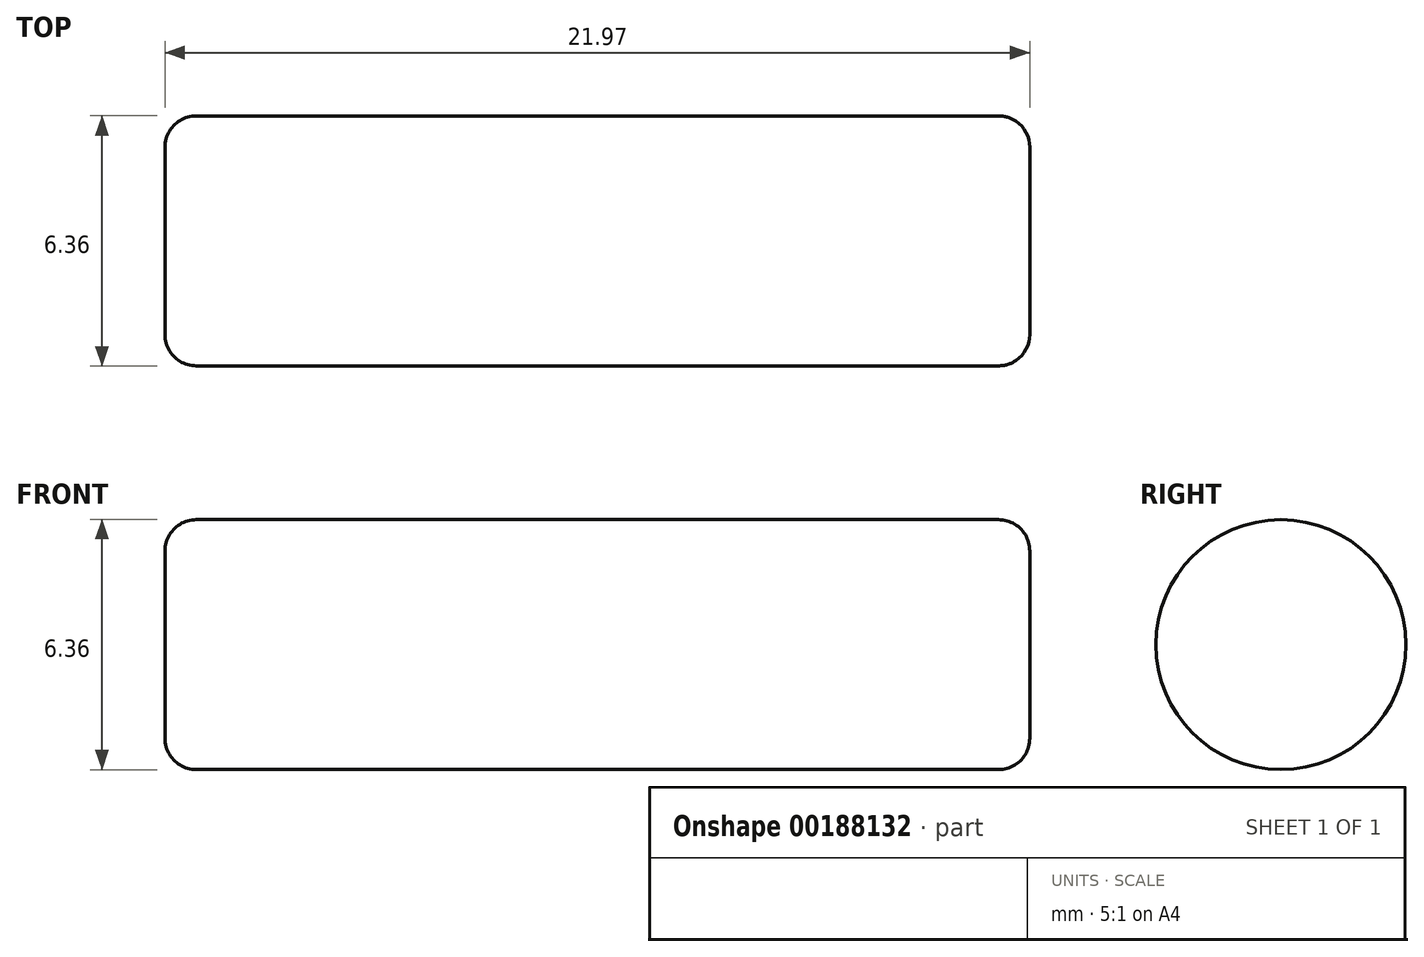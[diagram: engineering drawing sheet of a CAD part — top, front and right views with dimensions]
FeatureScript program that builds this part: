
annotation { "Feature Type Name" : "Feature", "Feature Type Description" : "" }
export const myFeature = defineFeature(function(context is Context, id is Id, definition is map)
    precondition{}
    {
        {
            var Q0;
            Q0=qCreatedBy(makeId("Right.planeOp"),FACE);
            var sketch = newSketch(context, id + "F0", { "sketchPlane" : qUnion([Q0])});
            skCircle(sketch, "E0", {"center": v(0, 0) * mm, "radius": 3.18 * mm});
            skSolve(sketch);
        }
        {
            var Q0;
            Q0 = qSketchRegion(id + "F0", true);
            extrude(context, id + "F1", {"entities" : qUnion([Q0]), "depth" : 21.97 * mm});
        }
        {
            var Q0;
            Q0=makeQuery(id+"F1.opExtrude","CAP_EDGE",EDGE,{"disambiguationData":[OSD([sQuery(id+"F0.wireOp",EDGE,"E0")])],"isStart":false});
            var Q1;
            Q1=makeQuery(id+"F1.opExtrude","CAP_EDGE",EDGE,{"disambiguationData":[OSD([sQuery(id+"F0.wireOp",EDGE,"E0")])],"isStart":true});
            fillet(context, id + "F2", {"entities" : qUnion([Q0, Q1]), "radius" : 0.8 * mm, "tangentPropagation" : true, "allowEdgeOverflow" : false});
        }
    });
